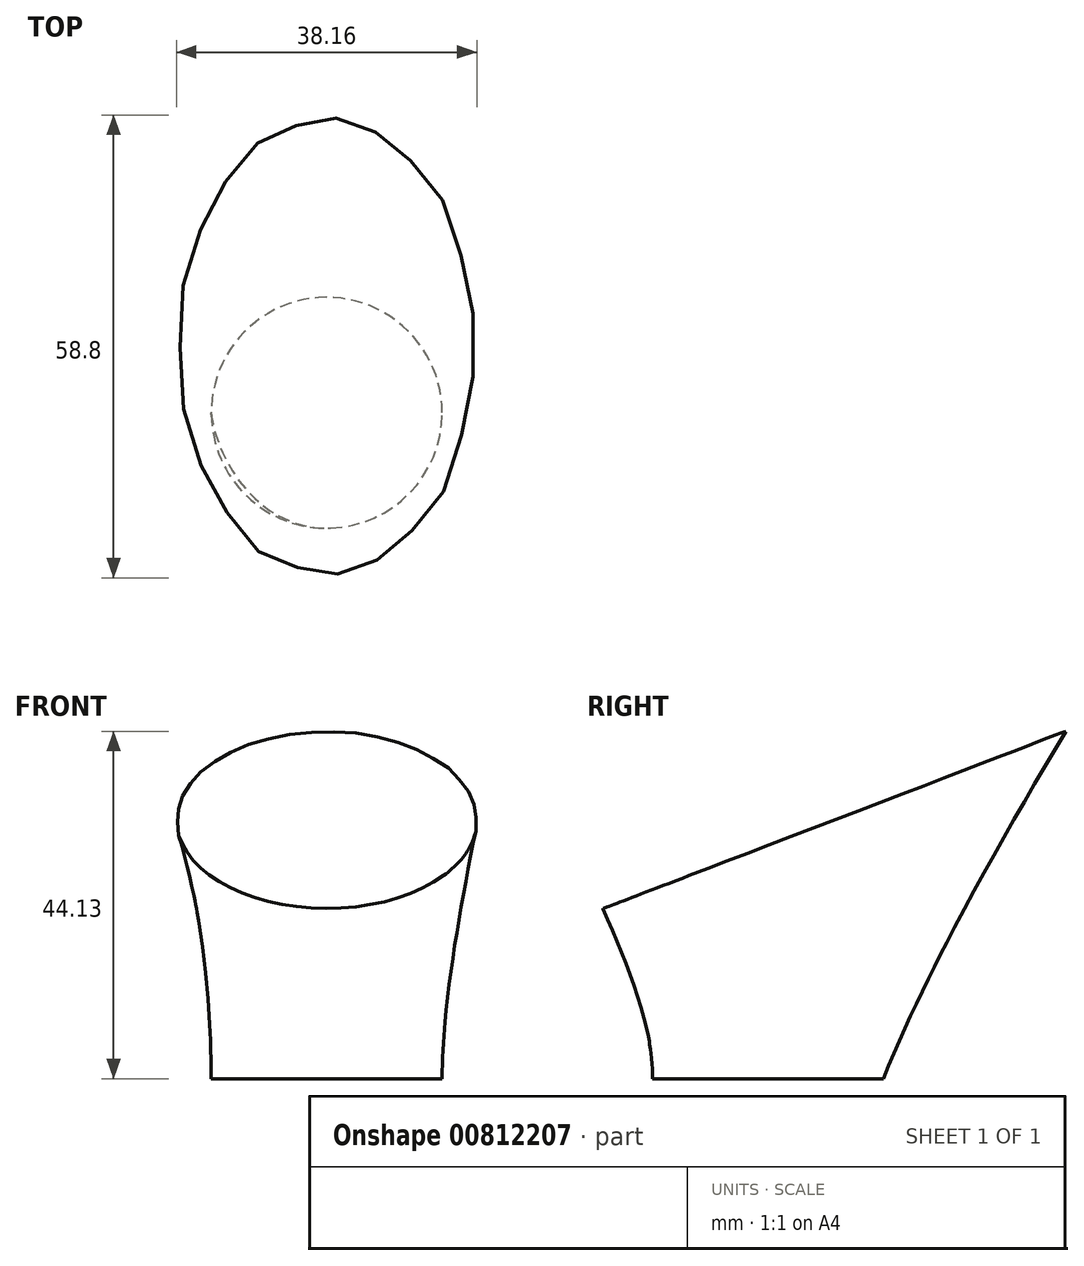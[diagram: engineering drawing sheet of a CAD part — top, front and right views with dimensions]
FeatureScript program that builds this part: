
annotation { "Feature Type Name" : "Feature", "Feature Type Description" : "" }
export const myFeature = defineFeature(function(context is Context, id is Id, definition is map)
    precondition{}
    {
        {
            var Q0;
            Q0=qCreatedBy(makeId("Right.planeOp"),FACE);
            var sketch = newSketch(context, id + "F0", { "sketchPlane" : qUnion([Q0])});
            skLineSegment(sketch, "E0", {"start": v(0, 0) * mm, "end": v(0, 127) * mm});
            skLineSegment(sketch, "E1", {"start": v(0, 127) * mm, "end": v(71.15, 154.28) * mm});
            skSolve(sketch);
        }
        {
            var Q0;
            Q0=sQuery(id+"F0.wireOp",EDGE,"E1");
            cPlane(context, id + "F1", {"entities" : qUnion([Q0]), "cplaneType" : CPlaneType.LINE_ANGLE, "offset" : 25.4 * mm, "angle" : 0 * degree, "width" : 152.4 * mm, "height" : 152.4 * mm});
        }
        {
            var Q0;
            Q0=qCreatedBy(id+"F1.planeOp",FACE);
            var sketch = newSketch(context, id + "F2", { "sketchPlane" : qUnion([Q0])});
            skEllipse(sketch, "E2", {"center": v(0, 45.02) * mm, "majorRadius": 31.49 * mm, "minorRadius": 19.08 * mm, "majorAxis": v(0, 1)});
            skSolve(sketch);
        }
        {
            var Q0;
            Q0=qCreatedBy(makeId("Top.planeOp"),FACE);
            cPlane(context, id + "F3", {"entities" : qUnion([Q0]), "cplaneType" : CPlaneType.OFFSET, "offset" : 12.7 * mm, "width" : 152.4 * mm, "height" : 152.4 * mm});
        }
        {
            var Q0;
            Q0=qCreatedBy(id+"F3.planeOp",FACE);
            cPlane(context, id + "F4", {"entities" : qUnion([Q0]), "cplaneType" : CPlaneType.OFFSET, "offset" : 81.28 * mm, "width" : 152.4 * mm, "height" : 152.4 * mm});
        }
        {
            var Q0;
            Q0=qCreatedBy(id+"F4.planeOp",FACE);
            var sketch = newSketch(context, id + "F5", { "sketchPlane" : qUnion([Q0])});
            skCircle(sketch, "E3", {"center": v(0, -8.85) * mm, "radius": 14.67 * mm});
            skSolve(sketch);
        }
        {
            var Q0;
            Q0=makeQuery(id+"F5.imprint","IMPRINT",FACE,{"disambiguationData":[TD([[makeQuery(id+"F5.imprint","IMPRINT",EDGE,{"derivedFrom":sQuery(id+"F5.wireOp",EDGE,"E3")}),1.0]])]});
            var Q1;
            Q1=makeQuery(id+"F2.imprint","IMPRINT",FACE,{"disambiguationData":[TD([[makeQuery(id+"F2.imprint","IMPRINT",EDGE,{"derivedFrom":sQuery(id+"F2.wireOp",EDGE,"E2")}),1.0]])]});
            loft(context, id + "F6", {"sheetProfilesArray" : [{ "sheetProfileEntities" : qUnion([Q0]) }, { "sheetProfileEntities" : qUnion([Q1]) }]});
        }
    });
